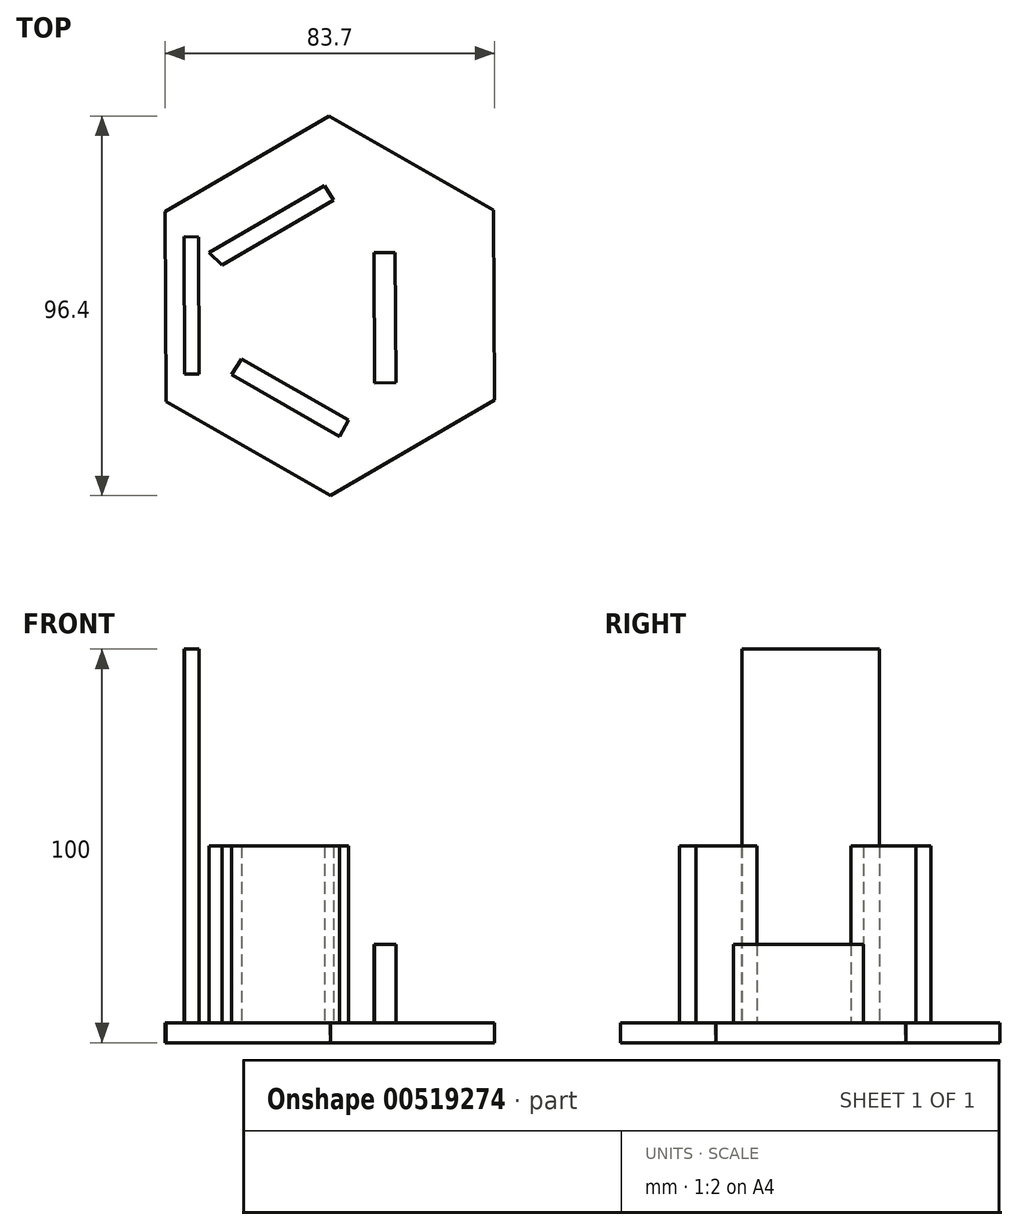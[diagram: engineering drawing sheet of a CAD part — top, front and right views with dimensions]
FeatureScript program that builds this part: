
annotation { "Feature Type Name" : "Feature", "Feature Type Description" : "" }
export const myFeature = defineFeature(function(context is Context, id is Id, definition is map)
    precondition{}
    {
        {
            var Q0;
            Q0=qCreatedBy(makeId("Top.planeOp"),FACE);
            var sketch = newSketch(context, id + "F0", { "sketchPlane" : qUnion([Q0])});
            skLineSegment(sketch, "E0.0", {"start": v(41.85, -23.91) * mm, "end": v(0.22, -48.2) * mm});
            skLineSegment(sketch, "E0.1", {"start": v(0.22, -48.2) * mm, "end": v(-41.63, -24.29) * mm});
            skLineSegment(sketch, "E0.2", {"start": v(-41.63, -24.29) * mm, "end": v(-41.85, 23.91) * mm});
            skLineSegment(sketch, "E0.3", {"start": v(-41.85, 23.91) * mm, "end": v(-0.22, 48.2) * mm});
            skLineSegment(sketch, "E0.4", {"start": v(-0.22, 48.2) * mm, "end": v(41.63, 24.29) * mm});
            skLineSegment(sketch, "E0.5", {"start": v(41.63, 24.29) * mm, "end": v(41.85, -23.91) * mm});
            skPoint(sketch, "E0.0.midPoint", {"position": v(21.03, -36.06) * mm});
            skLineSegment(sketch, "E1", {"start": v(-37, 17.55) * mm, "end": v(-36.85, -17.3) * mm});
            skLineSegment(sketch, "E2", {"start": v(-36.85, -17.3) * mm, "end": v(-33.2, -17.3) * mm});
            skLineSegment(sketch, "E3", {"start": v(-33.2, -17.3) * mm, "end": v(-33.36, 17.52) * mm});
            skLineSegment(sketch, "E4", {"start": v(-33.36, 17.52) * mm, "end": v(-37, 17.55) * mm});
            skLineSegment(sketch, "E5", {"start": v(-30.67, 13.48) * mm, "end": v(-1.31, 30.61) * mm});
            skLineSegment(sketch, "E6", {"start": v(-1.31, 30.61) * mm, "end": v(0.9, 26.83) * mm});
            skLineSegment(sketch, "E7", {"start": v(0.9, 26.83) * mm, "end": v(-27.3, 10.38) * mm});
            skLineSegment(sketch, "E8", {"start": v(-27.3, 10.38) * mm, "end": v(-30.67, 13.48) * mm});
            skLineSegment(sketch, "E9", {"start": v(-25, -17.5) * mm, "end": v(2.44, -33.17) * mm});
            skLineSegment(sketch, "E10", {"start": v(2.44, -33.17) * mm, "end": v(4.8, -29.04) * mm});
            skLineSegment(sketch, "E11", {"start": v(4.8, -29.04) * mm, "end": v(-22.38, -13.51) * mm});
            skLineSegment(sketch, "E12", {"start": v(-22.38, -13.51) * mm, "end": v(-25, -17.5) * mm});
            skLineSegment(sketch, "E13", {"start": v(16.63, 13.48) * mm, "end": v(16.78, -19.53) * mm});
            skLineSegment(sketch, "E14", {"start": v(16.78, -19.53) * mm, "end": v(11.36, -19.55) * mm});
            skLineSegment(sketch, "E15", {"start": v(11.36, -19.55) * mm, "end": v(11.2, 13.48) * mm});
            skLineSegment(sketch, "E16", {"start": v(11.2, 13.48) * mm, "end": v(16.63, 13.48) * mm});
            skSolve(sketch);
        }
        {
            var Q0;
            Q0=makeQuery(id+"F0.imprint","IMPRINT",FACE,{"disambiguationData":[TD([[makeQuery(id+"F0.imprint","IMPRINT",EDGE,{"derivedFrom":sQuery(id+"F0.wireOp",EDGE,"E1")}),1.0]])]});
            extrude(context, id + "F1", {"entities" : qUnion([Q0]), "depth" : 100 * mm, "offsetDistance" : 25 * mm});
        }
        {
            var Q0;
            Q0=makeQuery(id+"F0.imprint","IMPRINT",FACE,{"disambiguationData":[TD([[makeQuery(id+"F0.imprint","IMPRINT",EDGE,{"derivedFrom":sQuery(id+"F0.wireOp",EDGE,"E0.0")}),-1.0]])]});
            extrude(context, id + "F2", {"entities" : qUnion([Q0]), "operationType" : NewBodyOperationType.ADD, "depth" : 5 * mm, "offsetDistance" : 25 * mm});
        }
        {
            var Q0;
            Q0=makeQuery(id+"F0.imprint","IMPRINT",FACE,{"disambiguationData":[TD([[makeQuery(id+"F0.imprint","IMPRINT",EDGE,{"derivedFrom":sQuery(id+"F0.wireOp",EDGE,"E5")}),-1.0]])]});
            var Q1;
            Q1=makeQuery(id+"F0.imprint","IMPRINT",FACE,{"disambiguationData":[TD([[makeQuery(id+"F0.imprint","IMPRINT",EDGE,{"derivedFrom":sQuery(id+"F0.wireOp",EDGE,"E9")}),1.0]])]});
            extrude(context, id + "F3", {"entities" : qUnion([Q0, Q1]), "operationType" : NewBodyOperationType.ADD, "depth" : 50 * mm, "offsetDistance" : 25 * mm});
        }
        {
            var Q0;
            Q0=makeQuery(id+"F0.imprint","IMPRINT",FACE,{"disambiguationData":[TD([[makeQuery(id+"F0.imprint","IMPRINT",EDGE,{"derivedFrom":sQuery(id+"F0.wireOp",EDGE,"E13")}),-1.0]])]});
            extrude(context, id + "F4", {"entities" : qUnion([Q0]), "operationType" : NewBodyOperationType.ADD, "depth" : 25 * mm, "offsetDistance" : 25 * mm});
        }
    });
